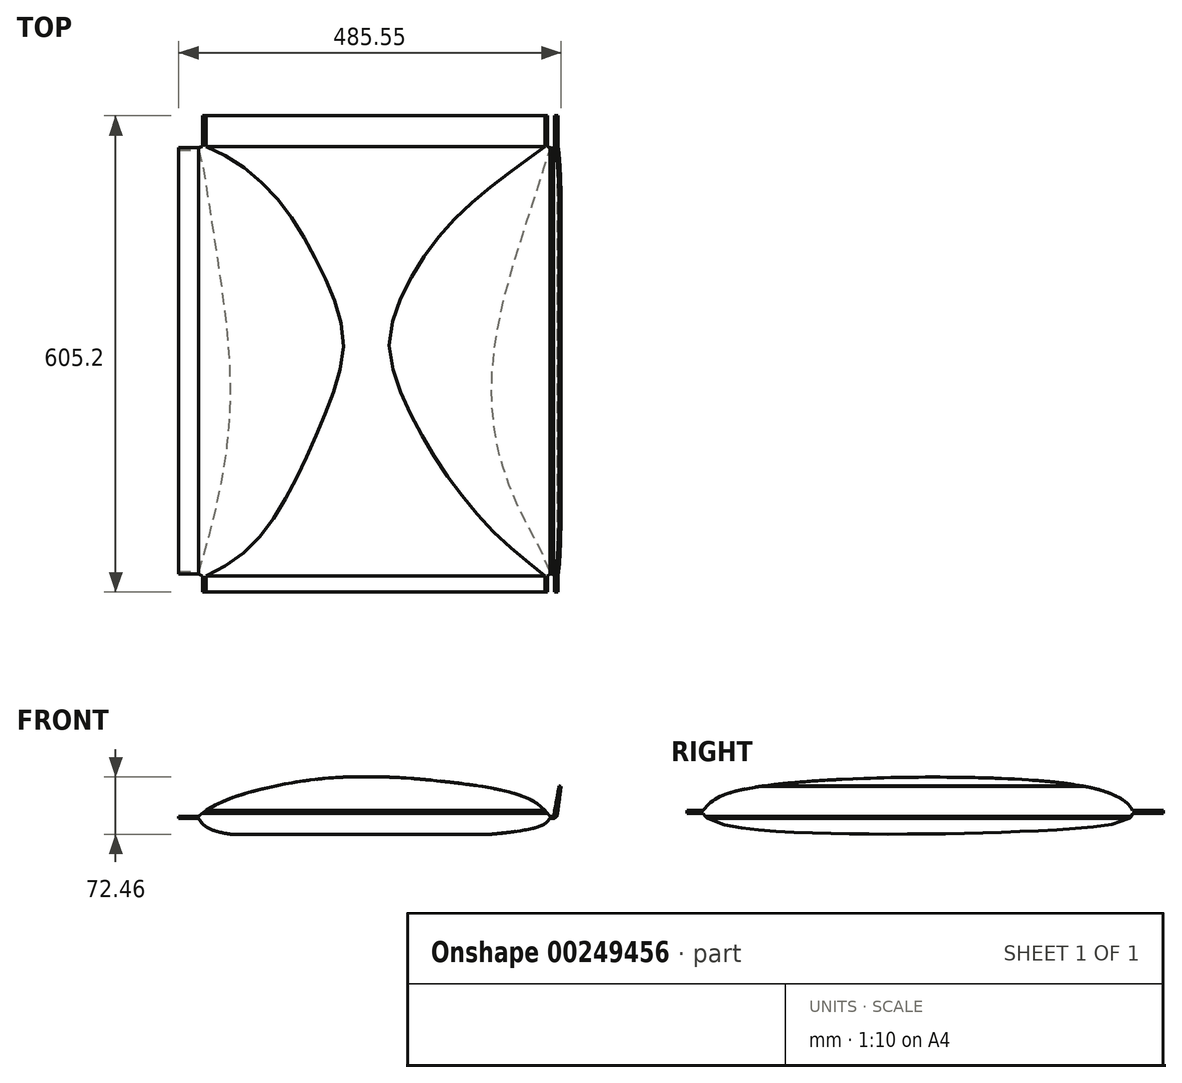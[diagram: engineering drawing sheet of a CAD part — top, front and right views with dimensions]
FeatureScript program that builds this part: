
annotation { "Feature Type Name" : "Feature", "Feature Type Description" : "" }
export const myFeature = defineFeature(function(context is Context, id is Id, definition is map)
    precondition{}
    {
        {
            var Q0;
            Q0=qCreatedBy(makeId("Front.planeOp"),FACE);
            var sketch = newSketch(context, id + "F0", { "sketchPlane" : qUnion([Q0])});
            skLineSegment(sketch, "E0", {"start": v(266.62, -0.85) * mm, "end": v(272.15, -0.85) * mm});
            skLineSegment(sketch, "E1", {"start": v(271.57, 1.71) * mm, "end": v(266.62, 2.15) * mm});
            skFitSpline(sketch, "E2", {"points": [v(266.62, 2.15) * mm, v(242.58, 23.2) * mm, v(126.27, 46.87) * mm, v(-30.7, 48.93) * mm, v(-151.65, 19.6) * mm, v(-179.44, 2.15) * mm], "startDerivative": vector(-144.3, 181.7) * mm, "endDerivative": vector(-175.5, -138.36) * mm});
            skFitSpline(sketch, "E3", {"points": [v(266.62, -0.85) * mm, v(245.15, -13.35) * mm, v(-151.13, -18.5) * mm, v(-179.44, -0.85) * mm], "startDerivative": vector(-54.29, -80.4) * mm, "endDerivative": vector(-63.63, 103.53) * mm});
            skLineSegment(sketch, "E4", {"start": v(-179.44, 2.15) * mm, "end": v(-204.65, 2.15) * mm});
            skLineSegment(sketch, "E5", {"start": v(-179.44, -0.85) * mm, "end": v(-204.65, -0.85) * mm});
            skLineSegment(sketch, "E6", {"start": v(-204.65, -0.85) * mm, "end": v(-204.65, 2.15) * mm});
            skLineSegment(sketch, "E7", {"start": v(271.57, 1.71) * mm, "end": v(278.42, 40.45) * mm});
            skLineSegment(sketch, "E8", {"start": v(278.42, 40.45) * mm, "end": v(280.9, 40.01) * mm});
            skLineSegment(sketch, "E9", {"start": v(272.15, -0.85) * mm, "end": v(275.8, 1.93) * mm});
            skPoint(sketch, "E9.endSnap0", {"position": v(269.1, 1.93) * mm});
            skLineSegment(sketch, "E10", {"start": v(275.8, 1.93) * mm, "end": v(280.9, 40.01) * mm});
            skSolve(sketch);
        }
        {
            var Q0;
            Q0 = qSketchRegion(id + "F0", true);
            extrude(context, id + "F1", {"entities" : qUnion([Q0]), "oppositeDirection" : true, "depth" : 600 * mm, "hasSecondDirection" : true, "secondDirectionOppositeDirection" : false, "secondDirectionDepth" : 170 * mm});
        }
        {
            var Q0;
            Q0=qCreatedBy(makeId("Right.planeOp"),FACE);
            var sketch = newSketch(context, id + "F2", { "sketchPlane" : qUnion([Q0])});
            skLineSegment(sketch, "E11", {"start": v(-84.59, 9.21) * mm, "end": v(-105.16, 9.21) * mm});
            skLineSegment(sketch, "E12", {"start": v(-105.16, 9.21) * mm, "end": v(-105.16, 5.91) * mm});
            skLineSegment(sketch, "E13", {"start": v(-105.16, 5.91) * mm, "end": v(-84.59, 5.91) * mm});
            skLineSegment(sketch, "E14", {"start": v(460.92, 5.91) * mm, "end": v(500.04, 5.91) * mm});
            skLineSegment(sketch, "E15", {"start": v(500.04, 5.91) * mm, "end": v(500.04, 9.21) * mm});
            skLineSegment(sketch, "E16", {"start": v(500.04, 9.21) * mm, "end": v(460.92, 9.21) * mm});
            skFitSpline(sketch, "E17", {"points": [v(-84.59, 9.21) * mm, v(-75.18, 19.45) * mm, v(-17.6, 39.13) * mm, v(397.04, 40.59) * mm, v(455.69, 16.73) * mm, v(460.92, 9.21) * mm], "startDerivative": vector(92.72, 117.93) * mm, "endDerivative": vector(56.43, -101) * mm});
            skFitSpline(sketch, "E18", {"points": [v(460.92, 5.91) * mm, v(457.55, 0) * mm, v(396.27, -12.73) * mm, v(-17.6, -15.1) * mm, v(-79.93, 0) * mm, v(-84.59, 5.91) * mm], "startDerivative": vector(-33.06, -97.24) * mm, "endDerivative": vector(-51.48, 89.8) * mm});
            skLineSegment(sketch, "E19.bottom", {"start": v(-205.97, 126.06) * mm, "end": v(646.65, 126.06) * mm});
            skLineSegment(sketch, "E19.top", {"start": v(-205.97, -102.76) * mm, "end": v(646.65, -102.76) * mm});
            skLineSegment(sketch, "E19.left", {"start": v(-205.97, 126.06) * mm, "end": v(-205.97, -102.76) * mm});
            skLineSegment(sketch, "E19.right", {"start": v(646.65, 126.06) * mm, "end": v(646.65, -102.76) * mm});
            skSolve(sketch);
        }
        {
            var Q0;
            Q0=makeQuery(id+"F2.imprint","IMPRINT",FACE,{"disambiguationData":[TD([[makeQuery(id+"F2.imprint","IMPRINT",EDGE,{"derivedFrom":sQuery(id+"F2.wireOp",EDGE,"E11")}),-1.0]])]});
            extrude(context, id + "F3", {"entities" : qUnion([Q0]), "operationType" : NewBodyOperationType.REMOVE, "endBound" : BoundingType.THROUGH_ALL, "oppositeDirection" : true, "depth" : 25 * mm, "hasSecondDirection" : true, "secondDirectionBound" : SecondDirectionBoundingType.THROUGH_ALL, "secondDirectionOppositeDirection" : false, "secondDirectionDepth" : 25 * mm});
        }
    });
